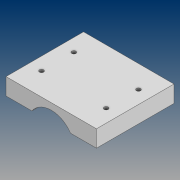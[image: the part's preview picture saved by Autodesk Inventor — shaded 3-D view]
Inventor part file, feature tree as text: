
AUTODESK INVENTOR PART (.ipt)
format: ipt  version: 2021 (Build 250183000, 183)  size: 106,496 bytes
history: native  units: mm
features: sketch x2, projected_geometry x2, extrude x1, hole x1
ambient origin geometry x8: Origin, YZ Plane, XZ Plane, XY Plane, X Axis, Y Axis, Z Axis, Center Point
bodies: Solid1 (feature_tree)
feature tree (6):
  extrude  "Extrusion1"  Depth=10.0mm
  hole  "Hole1"  [1 undecoded]
  sketch  "Sketch1"  dims[d0=36.0mm d1=10.0mm]
  sketch  "Sketch2"  dims[d2=70.0mm d3=13.0mm d4=60.0mm d5=0.0mm d6=25.0mm d7=3.2mm d8=6.0mm d9=4.0mm d10=2.0mm d11=90.0deg d12=8.0mm d13=20.594885mm]
  projected_geometry  "Projected Loop1"
  projected_geometry  "Projected Loop2"
note: 1 required parameter value undecoded (feature->parameter linkage not recoverable at this tier; creation-order binding heuristic only, values carry confidence <= 0.55)
